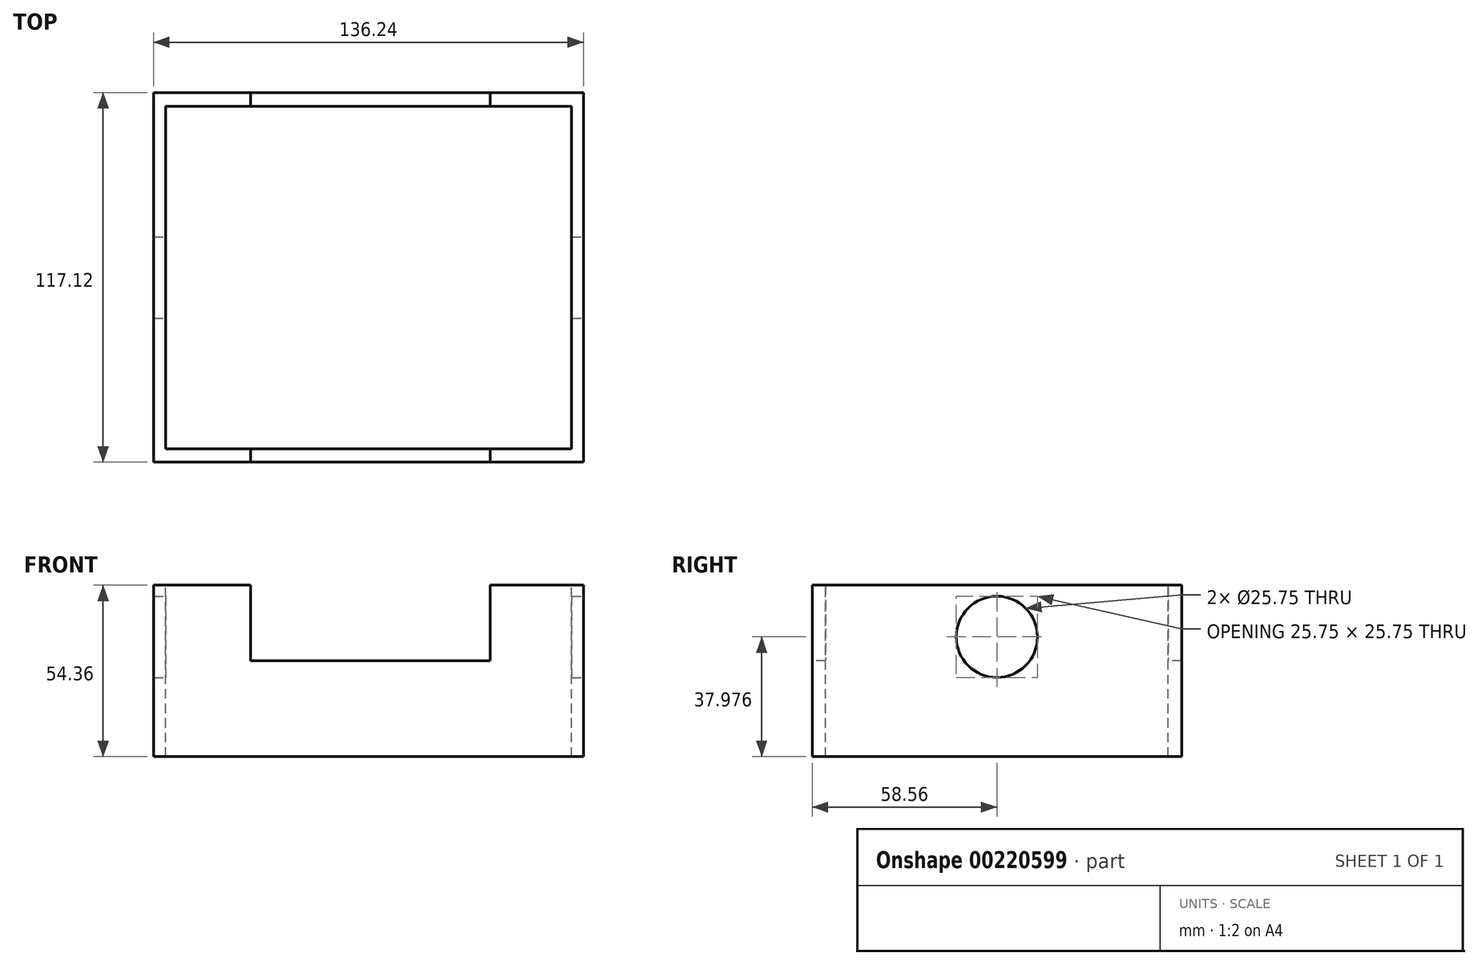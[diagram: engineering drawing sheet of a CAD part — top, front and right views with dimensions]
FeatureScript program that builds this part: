
annotation { "Feature Type Name" : "Feature", "Feature Type Description" : "" }
export const myFeature = defineFeature(function(context is Context, id is Id, definition is map)
    precondition{}
    {
        {
            var Q0;
            Q0=qCreatedBy(makeId("Top.planeOp"),FACE);
            var sketch = newSketch(context, id + "F0", { "sketchPlane" : qUnion([Q0])});
            skLineSegment(sketch, "E0.bottom", {"start": v(-68.12, 58.56) * mm, "end": v(68.12, 58.56) * mm});
            skLineSegment(sketch, "E0.top", {"start": v(-68.12, -58.56) * mm, "end": v(68.12, -58.56) * mm});
            skLineSegment(sketch, "E0.left", {"start": v(-68.12, 58.56) * mm, "end": v(-68.12, -58.56) * mm});
            skLineSegment(sketch, "E0.right", {"start": v(68.12, 58.56) * mm, "end": v(68.12, -58.56) * mm});
            skPoint(sketch, "E0.middle", {"position": v(0, 0) * mm});
            skSolve(sketch);
        }
        {
            var Q0;
            Q0=makeQuery(id+"F0.imprint","IMPRINT",FACE,{"disambiguationData":[TD([[makeQuery(id+"F0.imprint","IMPRINT",EDGE,{"derivedFrom":sQuery(id+"F0.wireOp",EDGE,"E0.bottom")}),-1.0]])]});
            extrude(context, id + "F1", {"entities" : qUnion([Q0]), "depth" : 54.36 * mm});
        }
        {
            var Q0;
            Q0=makeQuery(id+"F1.opExtrude","CAP_FACE",FACE,{"disambiguationData":[OSD([sQuery(id+"F0.wireOp",EDGE,"E0.bottom"),sQuery(id+"F0.wireOp",EDGE,"E0.top"),sQuery(id+"F0.wireOp",EDGE,"E0.left"),sQuery(id+"F0.wireOp",EDGE,"E0.right")])],"isStart":false});
            var sketch = newSketch(context, id + "F2", { "sketchPlane" : qUnion([Q0])});
            skLineSegment(sketch, "E1.bottom", {"start": v(-64.36, 54.27) * mm, "end": v(64.36, 54.27) * mm});
            skLineSegment(sketch, "E1.top", {"start": v(-64.36, -54.27) * mm, "end": v(64.36, -54.27) * mm});
            skLineSegment(sketch, "E1.left", {"start": v(-64.36, 54.27) * mm, "end": v(-64.36, -54.27) * mm});
            skLineSegment(sketch, "E1.right", {"start": v(64.36, 54.27) * mm, "end": v(64.36, -54.27) * mm});
            skPoint(sketch, "E1.middle", {"position": v(0, 0) * mm});
            skSolve(sketch);
        }
        {
            var Q0;
            Q0=makeQuery(id+"F2.imprint","IMPRINT",FACE,{"disambiguationData":[TD([[makeQuery(id+"F2.imprint","IMPRINT",EDGE,{"derivedFrom":sQuery(id+"F2.wireOp",EDGE,"E1.bottom")}),-1.0]])]});
            extrude(context, id + "F3", {"entities" : qUnion([Q0]), "operationType" : NewBodyOperationType.REMOVE, "endBound" : BoundingType.THROUGH_ALL, "oppositeDirection" : true, "depth" : 25.4 * mm});
        }
        {
            var Q0;
            Q0=makeQuery(id+"F1.opExtrude","SWEPT_FACE",FACE,{"disambiguationData":[OSD([sQuery(id+"F0.wireOp",EDGE,"E0.right")])]});
            var sketch = newSketch(context, id + "F4", { "sketchPlane" : qUnion([Q0])});
            skCircle(sketch, "E2", {"center": v(0, 37.98) * mm, "radius": 12.87 * mm});
            skSolve(sketch);
        }
        {
            var Q0;
            Q0=makeQuery(id+"F4.imprint","IMPRINT",FACE,{"disambiguationData":[TD([[makeQuery(id+"F4.imprint","IMPRINT",EDGE,{"derivedFrom":sQuery(id+"F4.wireOp",EDGE,"E2")}),1.0]])]});
            extrude(context, id + "F5", {"entities" : qUnion([Q0]), "operationType" : NewBodyOperationType.REMOVE, "endBound" : BoundingType.THROUGH_ALL, "oppositeDirection" : true, "depth" : 25.4 * mm});
        }
        {
            var Q0;
            Q0=makeQuery(id+"F1.opExtrude","SWEPT_FACE",FACE,{"disambiguationData":[OSD([sQuery(id+"F0.wireOp",EDGE,"E0.top")])]});
            var sketch = newSketch(context, id + "F6", { "sketchPlane" : qUnion([Q0])});
            skLineSegment(sketch, "E3.bottom", {"start": v(-37.4, 54.36) * mm, "end": v(38.56, 54.36) * mm});
            skLineSegment(sketch, "E3.top", {"start": v(-37.4, 30.44) * mm, "end": v(38.56, 30.44) * mm});
            skLineSegment(sketch, "E3.left", {"start": v(-37.4, 54.36) * mm, "end": v(-37.4, 30.44) * mm});
            skLineSegment(sketch, "E3.right", {"start": v(38.56, 54.36) * mm, "end": v(38.56, 30.44) * mm});
            skSolve(sketch);
        }
        {
            var Q0;
            Q0=makeQuery(id+"F6.imprint","IMPRINT",FACE,{"disambiguationData":[TD([[makeQuery(id+"F6.imprint","IMPRINT",EDGE,{"derivedFrom":sQuery(id+"F6.wireOp",EDGE,"E3.bottom")}),-1.0]])]});
            extrude(context, id + "F7", {"entities" : qUnion([Q0]), "operationType" : NewBodyOperationType.REMOVE, "endBound" : BoundingType.THROUGH_ALL, "oppositeDirection" : true, "depth" : 25.4 * mm});
        }
    });
